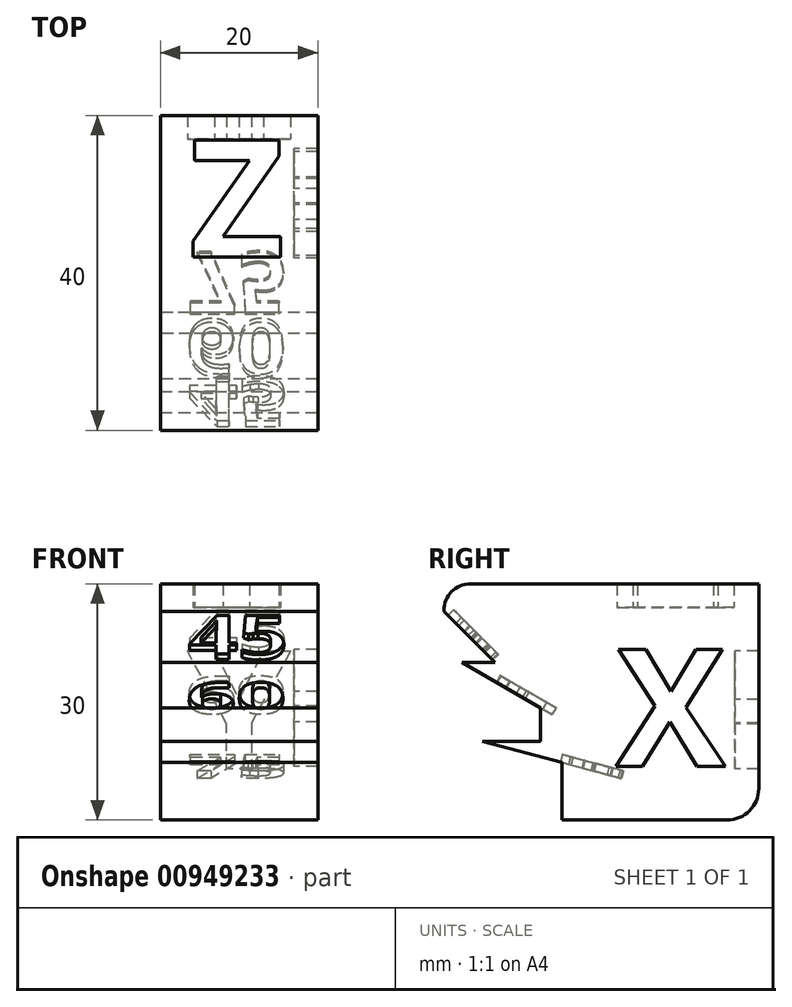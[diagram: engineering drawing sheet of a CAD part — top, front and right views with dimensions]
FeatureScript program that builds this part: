
annotation { "Feature Type Name" : "Feature", "Feature Type Description" : "" }
export const myFeature = defineFeature(function(context is Context, id is Id, definition is map)
    precondition{}
    {
        {
            var Q0;
            Q0=qCreatedBy(makeId("Top.planeOp"),FACE);
            var sketch = newSketch(context, id + "F0", { "sketchPlane" : qUnion([Q0])});
            skLineSegment(sketch, "E0.bottom", {"start": v(10, -15) * mm, "end": v(-10, -15) * mm});
            skLineSegment(sketch, "E0.top", {"start": v(10, 15) * mm, "end": v(-10, 15) * mm});
            skLineSegment(sketch, "E0.left", {"start": v(10, -15) * mm, "end": v(10, 15) * mm});
            skLineSegment(sketch, "E0.right", {"start": v(-10, -15) * mm, "end": v(-10, 15) * mm});
            skPoint(sketch, "E0.middle", {"position": v(0, 0) * mm});
            skText(sketch, "E1", { "text": "Z", "fontName": "OpenSans-Bold.ttf"});
            const initialGuessF0  = {"E1": [-0.00633, -0.003, 1, 0, 0.015]};
            skSetInitialGuess(sketch, initialGuessF0);
            skSolve(sketch);
        }
        {
            var Q0;
            Q0=makeQuery(id+"F0.imprint","IMPRINT",FACE,{"disambiguationData":[TD([[makeQuery(id+"F0.imprint","IMPRINT",EDGE,{"derivedFrom":sQuery(id+"F0.wireOp",EDGE,"E1.sketch_text.stroke-0")}),-1.0]])]});
            extrude(context, id + "F1", {"entities" : qUnion([Q0]), "depth" : 27 * mm, "offsetDistance" : 25 * mm});
        }
        {
            var Q0;
            Q0=makeQuery(id+"F0.imprint","IMPRINT",FACE,{"disambiguationData":[TD([[makeQuery(id+"F0.imprint","IMPRINT",EDGE,{"derivedFrom":sQuery(id+"F0.wireOp",EDGE,"E0.bottom")}),-1.0]])]});
            extrude(context, id + "F2", {"entities" : qUnion([Q0]), "operationType" : NewBodyOperationType.ADD, "depth" : 30 * mm, "offsetDistance" : 25 * mm});
        }
        {
            var Q0;
            Q0=qCreatedBy(makeId("Right.planeOp"),FACE);
            var sketch = newSketch(context, id + "F3", { "sketchPlane" : qUnion([Q0])});
            skText(sketch, "E2", { "text": "X", "fontName": "OpenSans-Bold.ttf"});
            const initialGuessF3  = {"E2": [-0.00313, 0.00682, 1, 0, 0.015]};
            skSetInitialGuess(sketch, initialGuessF3);
            skSolve(sketch);
        }
        {
            var Q0;
            Q0 = qSketchRegion(id + "F3", true);
            extrude(context, id + "F4", {"entities" : qUnion([Q0]), "operationType" : NewBodyOperationType.REMOVE, "depth" : 10 * mm, "offsetDistance" : 25 * mm, "hasSecondDirection" : true, "secondDirectionOppositeDirection" : true, "secondDirectionDepth" : -7 * mm});
        }
        {
            var Q0;
            Q0=qCreatedBy(makeId("Front.planeOp"),FACE);
            var sketch = newSketch(context, id + "F5", { "sketchPlane" : qUnion([Q0])});
            skText(sketch, "E3", { "text": "Y", "fontName": "OpenSans-Bold.ttf"});
            const initialGuessF5  = {"E3": [-0.00657, 0.00649, 1, 0, 0.01511]};
            skSetInitialGuess(sketch, initialGuessF5);
            skSolve(sketch);
        }
        {
            var Q0;
            Q0 = qSketchRegion(id + "F5", true);
            extrude(context, id + "F6", {"entities" : qUnion([Q0]), "operationType" : NewBodyOperationType.REMOVE, "oppositeDirection" : true, "depth" : 15 * mm, "offsetDistance" : 25 * mm, "hasSecondDirection" : true, "secondDirectionOppositeDirection" : true, "secondDirectionDepth" : 12 * mm});
        }
        {
            var Q0;
            Q0=makeQuery(id+"F2.opExtrude","SWEPT_FACE",FACE,{"disambiguationData":[OSD([sQuery(id+"F0.wireOp",EDGE,"E0.bottom")])]});
            extrude(context, id + "F7", {"entities" : qUnion([Q0]), "operationType" : NewBodyOperationType.ADD, "depth" : 10 * mm, "offsetDistance" : 25 * mm});
        }
        {
            var Q0;
            Q0=qCreatedBy(makeId("Right.planeOp"),FACE);
            var sketch = newSketch(context, id + "F8", { "sketchPlane" : qUnion([Q0])});
            skLineSegment(sketch, "E4.bottom", {"start": v(-25, 10) * mm, "end": v(-10, 10) * mm});
            skLineSegment(sketch, "E4.top", {"start": v(-25, 0) * mm, "end": v(-10, 0) * mm});
            skLineSegment(sketch, "E4.left", {"start": v(-25, 10) * mm, "end": v(-25, 0) * mm});
            skLineSegment(sketch, "E4.right", {"start": v(-10, 10) * mm, "end": v(-10, 0) * mm});
            skSolve(sketch);
        }
        {
            var Q0;
            Q0 = qSketchRegion(id + "F8", true);
            extrude(context, id + "F9", {"entities" : qUnion([Q0]), "operationType" : NewBodyOperationType.REMOVE, "depth" : 20 * mm, "offsetDistance" : 25 * mm, "symmetric" : true});
        }
        {
            var Q0;
            Q0=makeQuery(id+"F9.boolean.opBoolean","COPY",EDGE,{"derivedFrom":makeQuery(id+"F9.opExtrude","SWEPT_EDGE",EDGE,{"disambiguationData":[OSD([sQuery(id+"F8.wireOp",EDGE,"E4.bottom"),sQuery(id+"F8.wireOp",EDGE,"E4.right")])]})});
            chamfer(context, id + "F10", {"entities" : qUnion([Q0]), "chamferType" : ChamferType.OFFSET_ANGLE, "width" : 2.7 * mm, "oppositeDirection" : true, "angle" : 75 * degree, "tangentPropagation" : true});
        }
        {
            var Q0;
            Q0=makeQuery(id+"F10.opChamfer","BLEND_FACE",FACE,{"disambiguationData":[OSD([sQuery(id+"F8.wireOp",EDGE,"E4.bottom"),sQuery(id+"F8.wireOp",EDGE,"E4.right")])]});
            var Q1;
            Q1=makeQuery(id+"F10.opChamfer","BLEND_FACE",FACE,{"disambiguationData":[OSD([sQuery(id+"F8.wireOp",EDGE,"E4.bottom"),sQuery(id+"F8.wireOp",EDGE,"E4.right")])]});
            var sketch = newSketch(context, id + "F11", { "sketchPlane" : qUnion([Q0, Q1])});
            skText(sketch, "E5", { "text": "75\n", "fontName": "OpenSans-Bold.ttf"});
            const initialGuessF11  = {"E5": [-0.00656, 0.00383, 1, 0, 0.008]};
            skSetInitialGuess(sketch, initialGuessF11);
            skSolve(sketch);
        }
        {
            var Q0;
            Q0 = qSketchRegion(id + "F11", true);
            extrude(context, id + "F12", {"entities" : qUnion([Q0]), "operationType" : NewBodyOperationType.REMOVE, "oppositeDirection" : true, "depth" : 1 * mm, "offsetDistance" : 25 * mm});
        }
        {
            var Q0;
            Q0=qCreatedBy(makeId("Right.planeOp"),FACE);
            var sketch = newSketch(context, id + "F13", { "sketchPlane" : qUnion([Q0])});
            skLineSegment(sketch, "E6.bottom", {"start": v(-27.7, 20) * mm, "end": v(-12.7, 20) * mm});
            skLineSegment(sketch, "E6.top", {"start": v(-27.7, 10) * mm, "end": v(-12.7, 10) * mm});
            skLineSegment(sketch, "E6.left", {"start": v(-27.7, 20) * mm, "end": v(-27.7, 10) * mm});
            skLineSegment(sketch, "E6.right", {"start": v(-12.7, 20) * mm, "end": v(-12.7, 10) * mm});
            skSolve(sketch);
        }
        {
            var Q0;
            Q0 = qSketchRegion(id + "F13", true);
            extrude(context, id + "F14", {"entities" : qUnion([Q0]), "operationType" : NewBodyOperationType.REMOVE, "depth" : 20 * mm, "offsetDistance" : 25 * mm, "symmetric" : true});
        }
        {
            var Q0;
            Q0=makeQuery(id+"F14.boolean.opBoolean","COPY",EDGE,{"derivedFrom":makeQuery(id+"F14.opExtrude","SWEPT_EDGE",EDGE,{"disambiguationData":[OSD([sQuery(id+"F13.wireOp",EDGE,"E6.bottom"),sQuery(id+"F13.wireOp",EDGE,"E6.right")])]})});
            chamfer(context, id + "F15", {"entities" : qUnion([Q0]), "chamferType" : ChamferType.OFFSET_ANGLE, "width" : 10 * mm, "oppositeDirection" : false, "angle" : 30 * degree, "tangentPropagation" : true});
        }
        {
            var Q0;
            Q0=makeQuery(id+"F15.opChamfer","BLEND_FACE",FACE,{"disambiguationData":[OSD([sQuery(id+"F13.wireOp",EDGE,"E6.bottom"),sQuery(id+"F13.wireOp",EDGE,"E6.right")])]});
            var sketch = newSketch(context, id + "F16", { "sketchPlane" : qUnion([Q0])});
            skText(sketch, "E7", { "text": "60", "fontName": "OpenSans-Bold.ttf"});
            const initialGuessF16  = {"E7": [-0.00673, 0.01657, 1, 0, 0.008]};
            skSetInitialGuess(sketch, initialGuessF16);
            skSolve(sketch);
        }
        {
            var Q0;
            Q0 = qSketchRegion(id + "F16", true);
            extrude(context, id + "F17", {"entities" : qUnion([Q0]), "operationType" : NewBodyOperationType.REMOVE, "oppositeDirection" : true, "depth" : 1 * mm, "offsetDistance" : 25 * mm});
        }
        {
            var Q0;
            Q0=qCreatedBy(makeId("Right.planeOp"),FACE);
            var sketch = newSketch(context, id + "F18", { "sketchPlane" : qUnion([Q0])});
            skLineSegment(sketch, "E8.bottom", {"start": v(-25.97, 28) * mm, "end": v(-18.47, 28) * mm});
            skLineSegment(sketch, "E8.top", {"start": v(-25.97, 20) * mm, "end": v(-18.47, 20) * mm});
            skLineSegment(sketch, "E8.left", {"start": v(-25.97, 28) * mm, "end": v(-25.97, 20) * mm});
            skLineSegment(sketch, "E8.right", {"start": v(-18.47, 28) * mm, "end": v(-18.47, 20) * mm});
            skSolve(sketch);
        }
        {
            var Q0;
            Q0 = qSketchRegion(id + "F18", true);
            extrude(context, id + "F19", {"entities" : qUnion([Q0]), "operationType" : NewBodyOperationType.REMOVE, "depth" : 20 * mm, "offsetDistance" : 25 * mm, "symmetric" : true});
        }
        {
            var Q0;
            Q0=makeQuery(id+"F19.boolean.opBoolean","COPY",EDGE,{"derivedFrom":makeQuery(id+"F19.opExtrude","SWEPT_EDGE",EDGE,{"disambiguationData":[OSD([sQuery(id+"F18.wireOp",EDGE,"E8.bottom"),sQuery(id+"F18.wireOp",EDGE,"E8.right")])]})});
            chamfer(context, id + "F20", {"entities" : qUnion([Q0]), "chamferType" : ChamferType.OFFSET_ANGLE, "width" : 8 * mm, "oppositeDirection" : false, "angle" : 45 * degree, "tangentPropagation" : true});
        }
        {
            var Q0;
            Q0=makeQuery(id+"F20.opChamfer","BLEND_FACE",FACE,{"disambiguationData":[OSD([sQuery(id+"F18.wireOp",EDGE,"E8.bottom"),sQuery(id+"F18.wireOp",EDGE,"E8.right")])]});
            var sketch = newSketch(context, id + "F21", { "sketchPlane" : qUnion([Q0])});
            skText(sketch, "E9", { "text": "45", "fontName": "OpenSans-Bold.ttf"});
            const initialGuessF21  = {"E9": [-0.0065, 0.02777, 1, 0, 0.008]};
            skSetInitialGuess(sketch, initialGuessF21);
            skSolve(sketch);
        }
        {
            var Q0;
            Q0 = qSketchRegion(id + "F21", true);
            extrude(context, id + "F22", {"entities" : qUnion([Q0]), "operationType" : NewBodyOperationType.REMOVE, "oppositeDirection" : true, "depth" : 1 * mm, "offsetDistance" : 25 * mm});
        }
        {
            var Q0;
            {var subQ0=sQuery(id+"F0.wireOp",EDGE,"E0.bottom");Q0=makeQuery(id+"F7.opExtrude","CAP_EDGE",EDGE,{"disambiguationData":[OSD([subQ0]),TDD([makeQuery(id+"F2.opExtrude","CAP_EDGE",EDGE,{"disambiguationData":[OSD([subQ0])],"isStart":false})])],"isStart":false});}
            fillet(context, id + "F23", {"entities" : qUnion([Q0]), "radius" : 3.4 * mm, "tangentPropagation" : true, "allowEdgeOverflow" : false});
        }
        {
            var Q0;
            Q0=makeQuery(id+"F2.opExtrude","CAP_EDGE",EDGE,{"disambiguationData":[OSD([sQuery(id+"F0.wireOp",EDGE,"E0.top")])],"isStart":true});
            fillet(context, id + "F24", {"entities" : qUnion([Q0]), "radius" : 4 * mm, "tangentPropagation" : true, "allowEdgeOverflow" : false});
        }
    });
